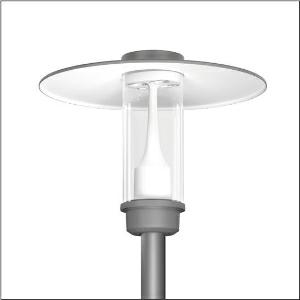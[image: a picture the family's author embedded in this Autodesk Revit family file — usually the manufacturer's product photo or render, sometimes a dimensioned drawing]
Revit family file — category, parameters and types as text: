
# Revit family: litepole_2_iq___p1_0a_5xa5425bf14h_a5ac
name_source: partatom
category: Lighting Fixtures
units: mm (PartAtom-declared; Revit-internal decimal feet)

## family parameters
Cut with Voids When Loaded = No
Host = Face
Light Source = No
Part Type = Normal
Room Calculation Point = No
Round Connector Dimension = Use Diameter
Shared = No

## types (1)
- --- (1 x LED, 1520 lm, 12.9 W, 2200K)
    Apparent Load = 13 VA
    CIE Flux Codes = 33 62 89 96 100
    Color Rendering = 70
    Color Temperature = 2200K
    Default Elevation = 1800 mm
    Description = Litepole 2 iQ, mast luminaire, Module 540 iQ-SR, primary light control with 3 zone facetted reflector, of plastic, silver coated, highly specular, structured, primary optical cover: cover, of PMMA, transparent, light distribution: P1.0a, light emission: direct distribution, primary light characteristic: strongly asymmetric, installation type: post-top, LED, High Power LED, rated luminous flux: 1.520lm, luminous efficacy: 118lm/W, light colour: 722, colour temperature: 2200K, control gear: ECG iQ, control: presetting dimming logarithmic, Street-Remote, Auto-Match, Temp-Guard, Lumen-Switch, Night-Set, Smart-Wire, Light-Fading, Desk-Remote (wireless, voltage-free reading and setting of iQ features in the workshop via application-optimized NFC function/RFID function), optimised constant luminous flux control (CLO 2.0), with terminal, 6-pole, max. 2.5mm², mains connection: 230..240V, AC, 50/60Hz, start of lifetime: 13W, end of service life: 13W, reduction: 6W, luminaire housing, upper part, of aluminium, coated, Siteco® metallic grey (DB 702S), diameter: 750mm, height: 590mm, spigot size: d x l = 76 x 70mm (post-top) | with reducer (optional accessory) 60 x 70mm, post-top mast mounting element, of diecast aluminium, coated, Siteco® metallic grey (DB 702S), Module 540 iQ-SR, traffic white (RAL 9016), equipment: standard, protection rating (complete): IP65, insulation class (complete): insulation class II (safety insulation), certification: CE, ENEC, VDE, packaging unit: 1 piece

Light Distribution: P1.0a
    Height = 590 mm
    Lamp = 1 x LED
    Lamp Light Flux = 1520 lm
    Lamp Power = 12.9 W
    Lamp count = 1
    Length = 750 mm
    Luminous efficacy = 118 lm/W
    Manufacturer = Siteco
    ModVariant = No
    Model = 5XA5425BF14H
    Number of Poles = 1
    OnlyDefault = Yes
    Power Factor = 1
    Product Name = Litepole 2 iQ | P1.0a
    Product group = mast luminaire | pylon top
    ProductGroupID = 6100
    Protection Class = Protection class II
    Protection Degree = IP 65
    RLX_Detail_Level = 1
    RLX_Emergency_Light_Flux = 0 lm
    RLX_Emergency_Type = 0
    RLX_Emergency_Type_DB = No
    RlxData = <blob elided: 138881 chars, md5=a18cfe1f>
    Socket = socket
    Standby Power = 0 W
    System Light Flux = 1520 lm
    System Power = 13 W
    Type Comments = factory setting: luminous flux: 100 % | dim-lin: 254 | 516 mA
    Type Image = l_1006518.jpg
    URL = http://relux.com
    VarID = @adj_145189
    Voltage = 0 V
    Weight = 0.00 kg
    Width = 0 mm  [stored 0 ft]

note: [stored X ft] marks values corroborated as IEEE doubles in the binary element streams (Revit-internal decimal feet)

## geometry (parser evidence)
native form markers: Blend x4, Sweep x10
no freeform markers — native parametric forms only
